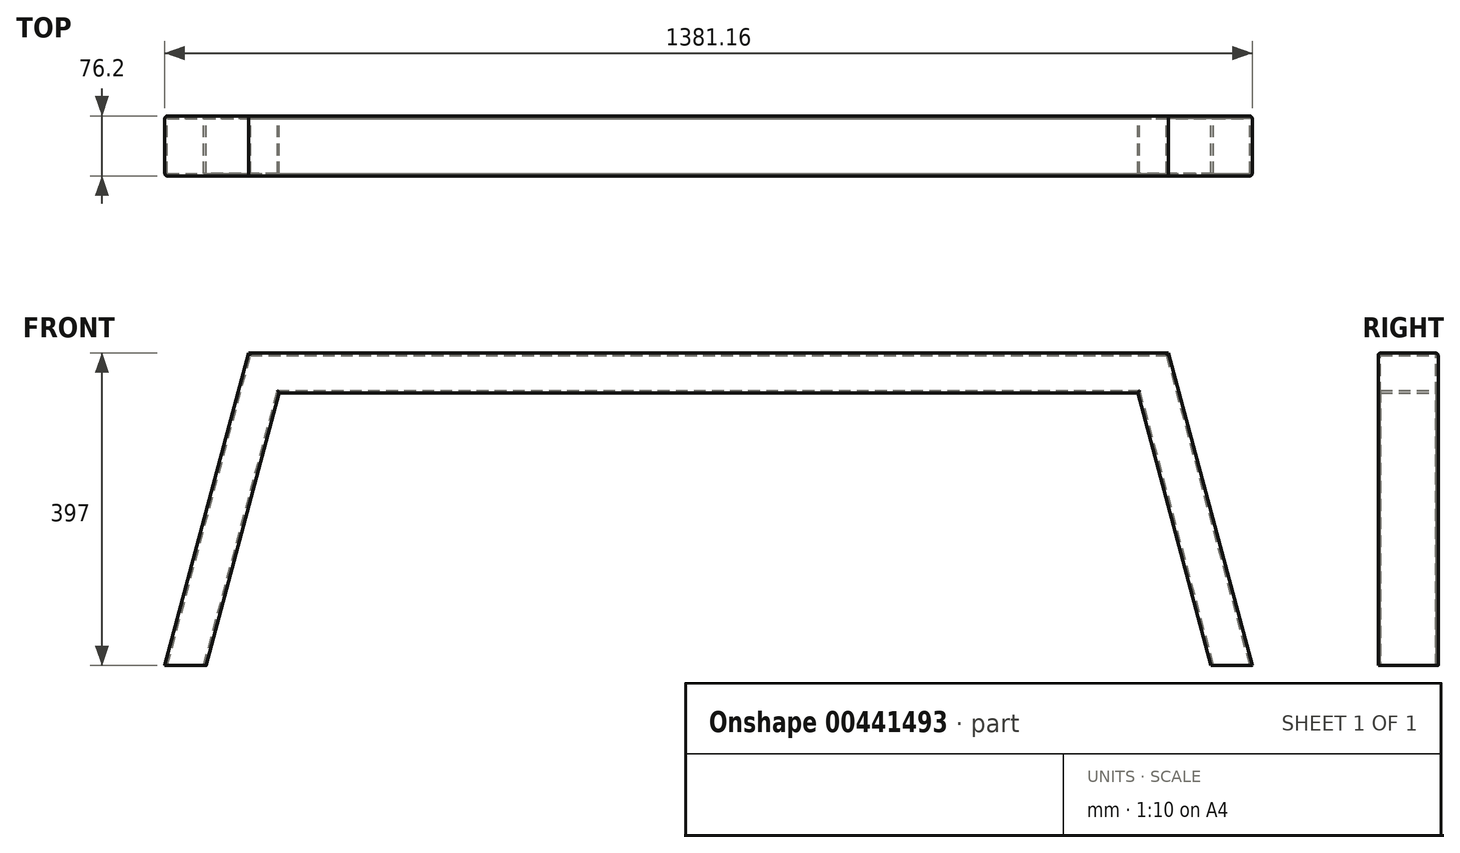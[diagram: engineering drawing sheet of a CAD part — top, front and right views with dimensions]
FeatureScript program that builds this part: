
annotation { "Feature Type Name" : "Feature", "Feature Type Description" : "" }
export const myFeature = defineFeature(function(context is Context, id is Id, definition is map)
    precondition{}
    {
        {
            var Q0;
            Q0=qCreatedBy(makeId("Front.planeOp"),FACE);
            var sketch = newSketch(context, id + "F0", { "sketchPlane" : qUnion([Q0])});
            skLineSegment(sketch, "E0", {"start": v(-690.58, -397) * mm, "end": v(-584.2, 0) * mm});
            skLineSegment(sketch, "E1", {"start": v(-584.2, 0) * mm, "end": v(584.2, 0) * mm});
            skLineSegment(sketch, "E2", {"start": v(584.2, 0) * mm, "end": v(690.58, -397) * mm});
            skLineSegment(sketch, "E3", {"start": v(-690.58, -397) * mm, "end": v(-637.98, -397) * mm});
            skLineSegment(sketch, "E4", {"start": v(-637.98, -397) * mm, "end": v(-545.22, -50.8) * mm});
            skLineSegment(sketch, "E5", {"start": v(-545.22, -50.8) * mm, "end": v(545.22, -50.8) * mm});
            skLineSegment(sketch, "E6", {"start": v(545.22, -50.8) * mm, "end": v(637.98, -397) * mm});
            skLineSegment(sketch, "E7", {"start": v(637.98, -397) * mm, "end": v(690.58, -397) * mm});
            skLineSegment(sketch, "E8", {"start": v(-545.22, -50.8) * mm, "end": v(-545.22, 0) * mm, "construction": true});
            skLineSegment(sketch, "E9", {"start": v(-545.22, -50.8) * mm, "end": v(-594.29, -37.65) * mm, "construction": true});
            skLineSegment(sketch, "E10", {"start": v(-690.58, -397) * mm, "end": v(-690.58, -400.05) * mm, "construction": true});
            skLineSegment(sketch, "E11", {"start": v(-545.22, 0) * mm, "end": v(-545.22, 19.05) * mm, "construction": true});
            skLineSegment(sketch, "E12", {"start": v(-545.22, 19.05) * mm, "end": v(-545.22, 57.15) * mm, "construction": true});
            skSolve(sketch);
        }
        {
            var Q0;
            Q0 = qSketchRegion(id + "F0", true);
            extrude(context, id + "F1", {"entities" : qUnion([Q0]), "endBound" : BoundingType.SYMMETRIC, "depth" : 76.2 * mm});
        }
        {
            var Q0;
            Q0=makeQuery(id+"F1.opExtrude","CAP_EDGE",EDGE,{"disambiguationData":[OSD([sQuery(id+"F0.wireOp",EDGE,"E0")])],"isStart":false});
            var Q1;
            Q1=makeQuery(id+"F1.opExtrude","CAP_EDGE",EDGE,{"disambiguationData":[OSD([sQuery(id+"F0.wireOp",EDGE,"E4")])],"isStart":false});
            var Q2;
            Q2=makeQuery(id+"F1.opExtrude","CAP_EDGE",EDGE,{"disambiguationData":[OSD([sQuery(id+"F0.wireOp",EDGE,"E0")])],"isStart":true});
            var Q3;
            Q3=makeQuery(id+"F1.opExtrude","CAP_EDGE",EDGE,{"disambiguationData":[OSD([sQuery(id+"F0.wireOp",EDGE,"E6")])],"isStart":true});
            var Q4;
            Q4=makeQuery(id+"F1.opExtrude","CAP_EDGE",EDGE,{"disambiguationData":[OSD([sQuery(id+"F0.wireOp",EDGE,"E6")])],"isStart":false});
            var Q5;
            Q5=makeQuery(id+"F1.opExtrude","CAP_EDGE",EDGE,{"disambiguationData":[OSD([sQuery(id+"F0.wireOp",EDGE,"E5")])],"isStart":false});
            var Q6;
            Q6=makeQuery(id+"F1.opExtrude","CAP_EDGE",EDGE,{"disambiguationData":[OSD([sQuery(id+"F0.wireOp",EDGE,"E1")])],"isStart":false});
            var Q7;
            Q7=makeQuery(id+"F1.opExtrude","CAP_EDGE",EDGE,{"disambiguationData":[OSD([sQuery(id+"F0.wireOp",EDGE,"E1")])],"isStart":true});
            var Q8;
            Q8=makeQuery(id+"F1.opExtrude","CAP_EDGE",EDGE,{"disambiguationData":[OSD([sQuery(id+"F0.wireOp",EDGE,"E4")])],"isStart":true});
            var Q9;
            Q9=makeQuery(id+"F1.opExtrude","CAP_EDGE",EDGE,{"disambiguationData":[OSD([sQuery(id+"F0.wireOp",EDGE,"E5")])],"isStart":true});
            var Q10;
            Q10=makeQuery(id+"F1.opExtrude","CAP_EDGE",EDGE,{"disambiguationData":[OSD([sQuery(id+"F0.wireOp",EDGE,"E2")])],"isStart":true});
            var Q11;
            Q11=makeQuery(id+"F1.opExtrude","CAP_EDGE",EDGE,{"disambiguationData":[OSD([sQuery(id+"F0.wireOp",EDGE,"E2")])],"isStart":false});
            fillet(context, id + "F2", {"entities" : qUnion([Q0, Q1, Q2, Q3, Q4, Q5, Q6, Q7, Q8, Q9, Q10, Q11]), "radius" : 3.17 * mm, "tangentPropagation" : true, "allowEdgeOverflow" : false});
        }
        {
            var Q0;
            Q0=makeQuery(id+"F1.opExtrude","SWEPT_FACE",FACE,{"disambiguationData":[OSD([sQuery(id+"F0.wireOp",EDGE,"E3")])]});
            var Q1;
            Q1=makeQuery(id+"F1.opExtrude","SWEPT_FACE",FACE,{"disambiguationData":[OSD([sQuery(id+"F0.wireOp",EDGE,"E7")])]});
            shell(context, id + "F3", {"entities" : qUnion([Q0, Q1]), "thickness" : 3.05 * mm});
        }
    });
